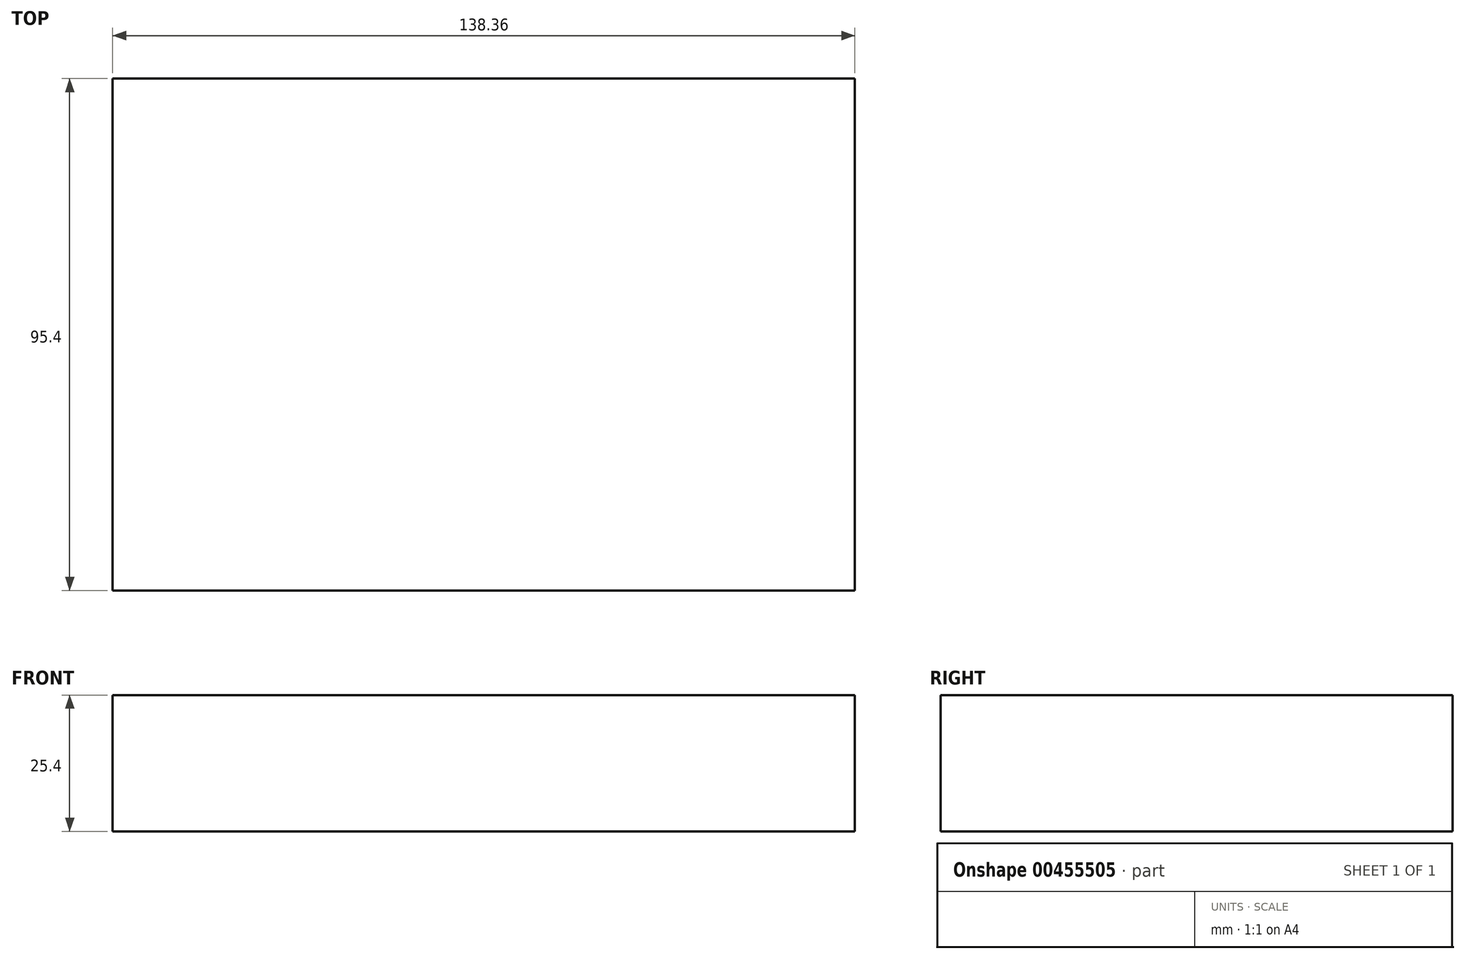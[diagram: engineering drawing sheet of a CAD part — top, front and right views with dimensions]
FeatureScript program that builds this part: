
annotation { "Feature Type Name" : "Feature", "Feature Type Description" : "" }
export const myFeature = defineFeature(function(context is Context, id is Id, definition is map)
    precondition{}
    {
        {
            var Q0;
            Q0=qCreatedBy(makeId("Top.planeOp"),FACE);
            var sketch = newSketch(context, id + "F0", { "sketchPlane" : qUnion([Q0])});
            skLineSegment(sketch, "E0.bottom", {"start": v(69.18, 47.7) * mm, "end": v(-69.18, 47.7) * mm});
            skLineSegment(sketch, "E0.top", {"start": v(69.18, -47.7) * mm, "end": v(-69.18, -47.7) * mm});
            skLineSegment(sketch, "E0.left", {"start": v(69.18, 47.7) * mm, "end": v(69.18, -47.7) * mm});
            skLineSegment(sketch, "E0.right", {"start": v(-69.18, 47.7) * mm, "end": v(-69.18, -47.7) * mm});
            skPoint(sketch, "E0.middle", {"position": v(0, 0) * mm});
            skSolve(sketch);
        }
        {
            var Q0;
            Q0 = qSketchRegion(id + "F0", true);
            extrude(context, id + "F1", {"entities" : qUnion([Q0]), "depth" : 25.4 * mm});
        }
    });
